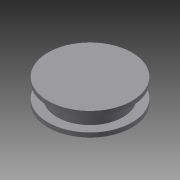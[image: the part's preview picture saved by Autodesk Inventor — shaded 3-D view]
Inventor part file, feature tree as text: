
AUTODESK INVENTOR PART (.ipt)
format: ipt  version: 2015 (Build 190159000, 159)  size: 86,016 bytes
history: native  units: mm
features: extrude x3, sketch x3
ambient origin geometry x8: Origin, YZ Plane, XZ Plane, XY Plane, X Axis, Y Axis, Z Axis, Center Point
bodies: Solid1 (feature_tree)
feature tree (6):
  extrude  "Extrusion1"  Depth=0.4mm TaperAngle=0.0deg
  extrude  "Extrusion2"  Depth=1.3mm TaperAngle=0.0deg
  extrude  "Extrusion3"  [1 undecoded]
  sketch  "Sketch1"  dims[d0=7.65mm d1=0.4mm d2=0.0mm]
  sketch  "Sketch2"  dims[d3=6.0mm d4=1.3mm d5=0.0mm]
  sketch  "Sketch3"  dims[d6=0.4mm d7=0.0mm]
note: 1 required parameter value undecoded (feature->parameter linkage not recoverable at this tier; creation-order binding heuristic only, values carry confidence <= 0.55)
